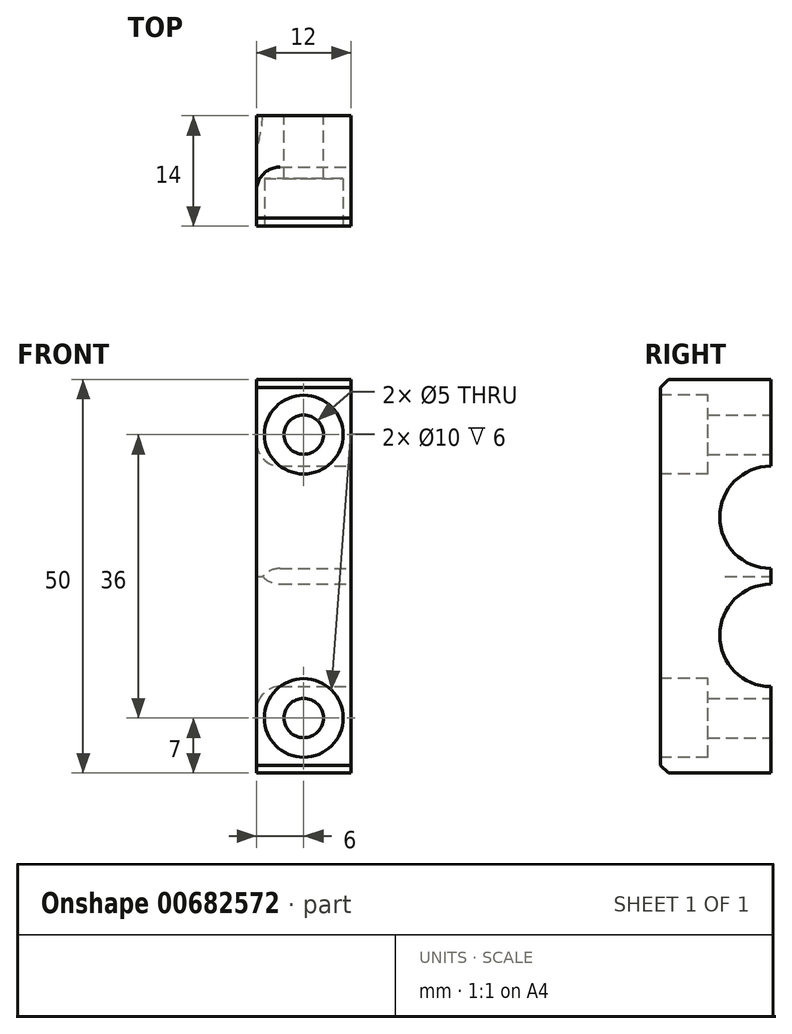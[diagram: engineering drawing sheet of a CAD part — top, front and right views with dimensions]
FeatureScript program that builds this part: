
annotation { "Feature Type Name" : "Feature", "Feature Type Description" : "" }
export const myFeature = defineFeature(function(context is Context, id is Id, definition is map)
    precondition{}
    {
        {
            var Q0;
            Q0=qCreatedBy(makeId("Front.planeOp"),FACE);
            var sketch = newSketch(context, id + "F0", { "sketchPlane" : qUnion([Q0])});
            skLineSegment(sketch, "E0.bottom", {"start": v(-6, 25) * mm, "end": v(6, 25) * mm});
            skLineSegment(sketch, "E0.top", {"start": v(-6, -25) * mm, "end": v(6, -25) * mm});
            skLineSegment(sketch, "E0.left", {"start": v(-6, 25) * mm, "end": v(-6, -25) * mm});
            skLineSegment(sketch, "E0.right", {"start": v(6, 25) * mm, "end": v(6, -25) * mm});
            skSolve(sketch);
        }
        {
            var Q0;
            Q0=qSketchRegion(id+"F0",true);
            extrude(context, id + "F1", {"entities" : qUnion([Q0]), "depth" : 30 * mm, "offsetDistance" : 25 * mm});
        }
        {
            var Q0;
            Q0=makeQuery(id+"F1.opExtrude","SWEPT_FACE",FACE,{"disambiguationData":[OSD([sQuery(id+"F0.wireOp",EDGE,"E0.right")])]});
            var sketch = newSketch(context, id + "F2", { "sketchPlane" : qUnion([Q0])});
            skCircle(sketch, "E1", {"center": v(-16, 7.5) * mm, "radius": 6.5 * mm});
            skCircle(sketch, "E2", {"center": v(-16, -7.5) * mm, "radius": 6.5 * mm});
            skSolve(sketch);
        }
        {
            var Q0;
            Q0=qSketchRegion(id+"F2",true);
            extrude(context, id + "F3", {"entities" : qUnion([Q0]), "operationType" : NewBodyOperationType.REMOVE, "endBound" : BoundingType.THROUGH_ALL, "oppositeDirection" : true, "depth" : 25 * mm, "offsetDistance" : 25 * mm});
        }
        {
            var Q0;
            Q0=qCreatedBy(makeId("Front.planeOp"),FACE);
            var sketch = newSketch(context, id + "F4", { "sketchPlane" : qUnion([Q0])});
            skLineSegment(sketch, "E3.bottom", {"start": v(-10, 25) * mm, "end": v(10, 25) * mm});
            skLineSegment(sketch, "E3.top", {"start": v(-10, -25) * mm, "end": v(10, -25) * mm});
            skLineSegment(sketch, "E3.left", {"start": v(-10, 25) * mm, "end": v(-10, -25) * mm});
            skLineSegment(sketch, "E3.right", {"start": v(10, 25) * mm, "end": v(10, -25) * mm});
            skPoint(sketch, "E4", {"position": v(0, 25) * mm});
            skSolve(sketch);
        }
        {
            var Q0;
            Q0=qSketchRegion(id+"F4",true);
            extrude(context, id + "F5", {"entities" : qUnion([Q0]), "operationType" : NewBodyOperationType.ADD, "depth" : 2 * mm, "offsetDistance" : 25 * mm});
        }
        {
            var Q0;
            Q0=makeQuery(id+"F3.boolean.opBoolean","INTERSECT",EDGE,{"derivedFrom":[makeQuery(id+"F1.opExtrude","SWEPT_FACE",FACE,{"disambiguationData":[OSD([sQuery(id+"F0.wireOp",EDGE,"E0.left")])]}),makeQuery(id+"F3.opExtrude","SWEPT_FACE",FACE,{"disambiguationData":[OSD([sQuery(id+"F2.wireOp",EDGE,"E1")])]})]});
            var Q1;
            Q1=makeQuery(id+"F3.boolean.opBoolean","INTERSECT",EDGE,{"derivedFrom":[makeQuery(id+"F1.opExtrude","SWEPT_FACE",FACE,{"disambiguationData":[OSD([sQuery(id+"F0.wireOp",EDGE,"E0.left")])]}),makeQuery(id+"F3.opExtrude","SWEPT_FACE",FACE,{"disambiguationData":[OSD([sQuery(id+"F2.wireOp",EDGE,"E2")])]})]});
            var Q2;
            Q2=makeQuery(id+"F3.boolean.opBoolean","COPY",EDGE,{"derivedFrom":makeQuery(id+"F3.opExtrude","CAP_EDGE",EDGE,{"disambiguationData":[OSD([sQuery(id+"F2.wireOp",EDGE,"E1")])],"isStart":true})});
            var Q3;
            Q3=makeQuery(id+"F3.boolean.opBoolean","COPY",EDGE,{"derivedFrom":makeQuery(id+"F3.opExtrude","CAP_EDGE",EDGE,{"disambiguationData":[OSD([sQuery(id+"F2.wireOp",EDGE,"E2")])],"isStart":true})});
            fillet(context, id + "F6", {"entities" : qUnion([Q0, Q1, Q2, Q3]), "radius" : 3 * mm, "tangentPropagation" : true, "allowEdgeOverflow" : false});
        }
        {
            var Q0;
            Q0=makeQuery(id+"F5.boolean.opBoolean","MERGE",FACE,{"derivedFrom":[makeQuery(id+"F1.opExtrude","CAP_FACE",FACE,{"disambiguationData":[OSD([sQuery(id+"F0.wireOp",EDGE,"E0.bottom"),sQuery(id+"F0.wireOp",EDGE,"E0.top"),sQuery(id+"F0.wireOp",EDGE,"E0.left"),sQuery(id+"F0.wireOp",EDGE,"E0.right")])],"isStart":true}),makeQuery(id+"F5.opExtrude","CAP_FACE",FACE,{"disambiguationData":[OSD([sQuery(id+"F4.wireOp",EDGE,"E3.bottom"),sQuery(id+"F4.wireOp",EDGE,"E3.top"),sQuery(id+"F4.wireOp",EDGE,"E3.left"),sQuery(id+"F4.wireOp",EDGE,"E3.right")])],"isStart":true})]});
            var sketch = newSketch(context, id + "F7", { "sketchPlane" : qUnion([Q0])});
            skPoint(sketch, "E5", {"position": v(0, 18) * mm});
            skPoint(sketch, "E6", {"position": v(0, -18) * mm});
            skSolve(sketch);
        }
        {
            var Q0;
            Q0=sQuery(id+"F7.wireOp",VERTEX,"E5");
            var Q1;
            Q1=sQuery(id+"F7.wireOp",VERTEX,"E6");
            var Q2;
            Q2=makeQuery(id+"F1.opExtrude","SWEPT_BODY",BODY,{"disambiguationData":[OSD([sQuery(id+"F0.wireOp",EDGE,"E0.bottom"),sQuery(id+"F0.wireOp",EDGE,"E0.top"),sQuery(id+"F0.wireOp",EDGE,"E0.left"),sQuery(id+"F0.wireOp",EDGE,"E0.right")])]});
            hole(context, id + "F8", {"style" : HoleStyle.SIMPLE, "endStyle" : HoleEndStyle.THROUGH, "holeDiameter" : 5 * mm, "majorDiameter" : 5 * mm, "isTappedThrough" : true, "tappedDepth" : 12 * mm, "tapClearance" : 3, "startFromSketch" : true, "locations" : qUnion([Q0, Q1]), "scope" : qUnion([Q2])});
        }
        {
            var Q0;
            Q0=makeQuery(id+"F5.boolean.opBoolean","MERGE",FACE,{"derivedFrom":[makeQuery(id+"F1.opExtrude","CAP_FACE",FACE,{"disambiguationData":[OSD([sQuery(id+"F0.wireOp",EDGE,"E0.bottom"),sQuery(id+"F0.wireOp",EDGE,"E0.top"),sQuery(id+"F0.wireOp",EDGE,"E0.left"),sQuery(id+"F0.wireOp",EDGE,"E0.right")])],"isStart":true}),makeQuery(id+"F5.opExtrude","CAP_FACE",FACE,{"disambiguationData":[OSD([sQuery(id+"F4.wireOp",EDGE,"E3.bottom"),sQuery(id+"F4.wireOp",EDGE,"E3.top"),sQuery(id+"F4.wireOp",EDGE,"E3.left"),sQuery(id+"F4.wireOp",EDGE,"E3.right")])],"isStart":true})]});
            var sketch = newSketch(context, id + "F9", { "sketchPlane" : qUnion([Q0])});
            skCircle(sketch, "E7.cCircle", {"center": v(0, 18) * mm, "radius": 5.89 * mm, "construction": true});
            skLineSegment(sketch, "E7.0", {"start": v(5.1, 15.06) * mm, "end": v(0, 12.11) * mm});
            skLineSegment(sketch, "E7.1", {"start": v(0, 12.11) * mm, "end": v(-5.1, 15.06) * mm});
            skLineSegment(sketch, "E7.2", {"start": v(-5.1, 15.06) * mm, "end": v(-5.1, 20.94) * mm});
            skLineSegment(sketch, "E7.3", {"start": v(-5.1, 20.94) * mm, "end": v(0, 23.89) * mm});
            skLineSegment(sketch, "E7.4", {"start": v(0, 23.89) * mm, "end": v(5.1, 20.94) * mm});
            skLineSegment(sketch, "E7.5", {"start": v(5.1, 20.94) * mm, "end": v(5.1, 15.06) * mm});
            skLineSegment(sketch, "E8.bottom", {"start": v(-5, 10) * mm, "end": v(5, 10) * mm});
            skLineSegment(sketch, "E8.top", {"start": v(-5, -10) * mm, "end": v(5, -10) * mm});
            skLineSegment(sketch, "E8.left", {"start": v(-5, 10) * mm, "end": v(-5, -10) * mm});
            skLineSegment(sketch, "E8.right", {"start": v(5, 10) * mm, "end": v(5, -10) * mm});
            skCircle(sketch, "E9.cCircle", {"center": v(0, -18) * mm, "radius": 5.89 * mm, "construction": true});
            skLineSegment(sketch, "E9.0", {"start": v(5.1, -15.06) * mm, "end": v(5.1, -20.94) * mm});
            skLineSegment(sketch, "E9.1", {"start": v(5.1, -20.94) * mm, "end": v(0, -23.89) * mm});
            skLineSegment(sketch, "E9.2", {"start": v(0, -23.89) * mm, "end": v(-5.1, -20.94) * mm});
            skLineSegment(sketch, "E9.3", {"start": v(-5.1, -20.94) * mm, "end": v(-5.1, -15.06) * mm});
            skLineSegment(sketch, "E9.4", {"start": v(-5.1, -15.06) * mm, "end": v(0, -12.11) * mm});
            skLineSegment(sketch, "E9.5", {"start": v(0, -12.11) * mm, "end": v(5.1, -15.06) * mm});
            skSolve(sketch);
        }
        {
            var Q0;
            Q0=qSketchRegion(id+"F9",true);
            extrude(context, id + "F10", {"entities" : qUnion([Q0]), "operationType" : NewBodyOperationType.REMOVE, "oppositeDirection" : true, "depth" : 8 * mm, "offsetDistance" : 25 * mm});
        }
        {
            var Q0;
            Q0=makeQuery(id+"F1.opExtrude","CAP_FACE",FACE,{"disambiguationData":[OSD([sQuery(id+"F0.wireOp",EDGE,"E0.bottom"),sQuery(id+"F0.wireOp",EDGE,"E0.top"),sQuery(id+"F0.wireOp",EDGE,"E0.left"),sQuery(id+"F0.wireOp",EDGE,"E0.right")])],"isStart":false});
            var sketch = newSketch(context, id + "F11", { "sketchPlane" : qUnion([Q0])});
            skCircle(sketch, "E10", {"center": v(0, 18) * mm, "radius": 5 * mm});
            skCircle(sketch, "E11", {"center": v(0, -18) * mm, "radius": 5 * mm});
            skSolve(sketch);
        }
        {
            var Q0;
            Q0=qSketchRegion(id+"F11",true);
            extrude(context, id + "F12", {"entities" : qUnion([Q0]), "operationType" : NewBodyOperationType.REMOVE, "oppositeDirection" : true, "depth" : 6 * mm, "offsetDistance" : 25 * mm});
        }
        {
            var Q0;
            Q0=makeQuery(id+"F1.opExtrude","CAP_EDGE",EDGE,{"disambiguationData":[OSD([sQuery(id+"F0.wireOp",EDGE,"E0.top")])],"isStart":false});
            var Q1;
            Q1=makeQuery(id+"F1.opExtrude","CAP_EDGE",EDGE,{"disambiguationData":[OSD([sQuery(id+"F0.wireOp",EDGE,"E0.bottom")])],"isStart":false});
            chamfer(context, id + "F13", {"entities" : qUnion([Q0, Q1]), "width" : 1 * mm, "tangentPropagation" : true});
        }
        {
            var Q0;
            Q0=qCreatedBy(makeId("Front.planeOp"),FACE);
            cPlane(context, id + "F14", {"entities" : qUnion([Q0]), "cplaneType" : CPlaneType.OFFSET, "offset" : 16 * mm, "width" : 150 * mm, "height" : 150 * mm});
        }
        {
            var Q0;
            Q0=qCreatedBy(id+"F14.planeOp",FACE);
            var sketch = newSketch(context, id + "F15", { "sketchPlane" : qUnion([Q0])});
            skLineSegment(sketch, "E12.bottom", {"start": v(-21.41, 33.65) * mm, "end": v(20.43, 33.65) * mm});
            skLineSegment(sketch, "E12.top", {"start": v(-21.41, -33.85) * mm, "end": v(20.43, -33.85) * mm});
            skLineSegment(sketch, "E12.left", {"start": v(-21.41, 33.65) * mm, "end": v(-21.41, -33.85) * mm});
            skLineSegment(sketch, "E12.right", {"start": v(20.43, 33.65) * mm, "end": v(20.43, -33.85) * mm});
            skSolve(sketch);
        }
        {
            var Q0;
            Q0 = qSketchRegion(id + "F15", true);
            extrude(context, id + "F16", {"entities" : qUnion([Q0]), "operationType" : NewBodyOperationType.REMOVE, "oppositeDirection" : true, "depth" : 25 * mm, "offsetDistance" : 25 * mm});
        }
    });
